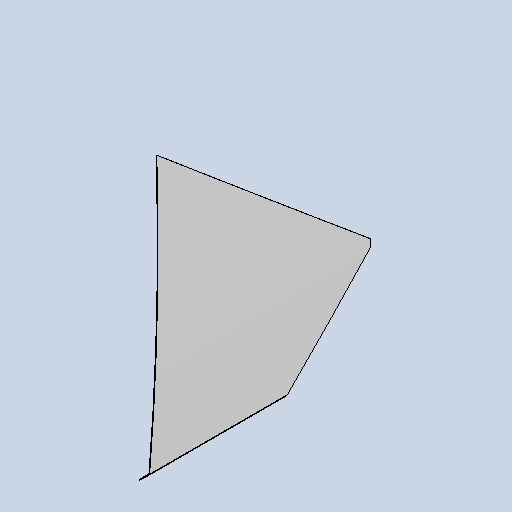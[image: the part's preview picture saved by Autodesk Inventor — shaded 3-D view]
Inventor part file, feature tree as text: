
AUTODESK INVENTOR PART (.ipt)
format: ipt  version: 2025 (Build 290162010, 162A)  size: 492,544 bytes
history: native  units: mm
features: other x4, sheet_metal_op x3, sketch x3, projected_geometry x3, extrude x1
ambient origin geometry x8: Origin, YZ Plane, XZ Plane, XY Plane, X Axis, Y Axis, Z Axis, Center Point
bodies: Body1 (feature_tree)
feature tree (14):
  sheet_metal_op  "Contour Flange2"
  extrude  "Extrusion3"  Depth=3.0mm
  other  "Mark5"
  other  "A-Side Definition"
  sketch  "Sketch1"  dims[d36=3.0mm d37=3.0mm]
  other  "Plate2"
  sheet_metal_op  "Bend2"
  sheet_metal_op  "Corner2"
  sketch  "Sketch5"  dims[d38=1.5mm]
  projected_geometry  "Projected Loop3"
  projected_geometry  "Projected Loop4"
  projected_geometry  "Projected Loop5"
  sketch  "Sketch8"  dims[d39=6.0mm d40=3.0mm d41=980.0mm d42=3.0mm d43=3.0mm d44=12.0mm d45=3.0mm d46=3.0mm d65=6.0mm d78=3.0mm d80=3.0mm d152=0.0mm d153=0.0mm d154=5.0mm d155=63.0mm d156=11050.0mm d157=23.736478mm d159=5.0mm d161=6.981317mm d162=6.981317mm d166=300.0mm d167=300.0mm d168=12.0mm d169=12.0mm d170=0.0mm d171=1843.0mm d172=566.0mm]
  other  "Definition1"
